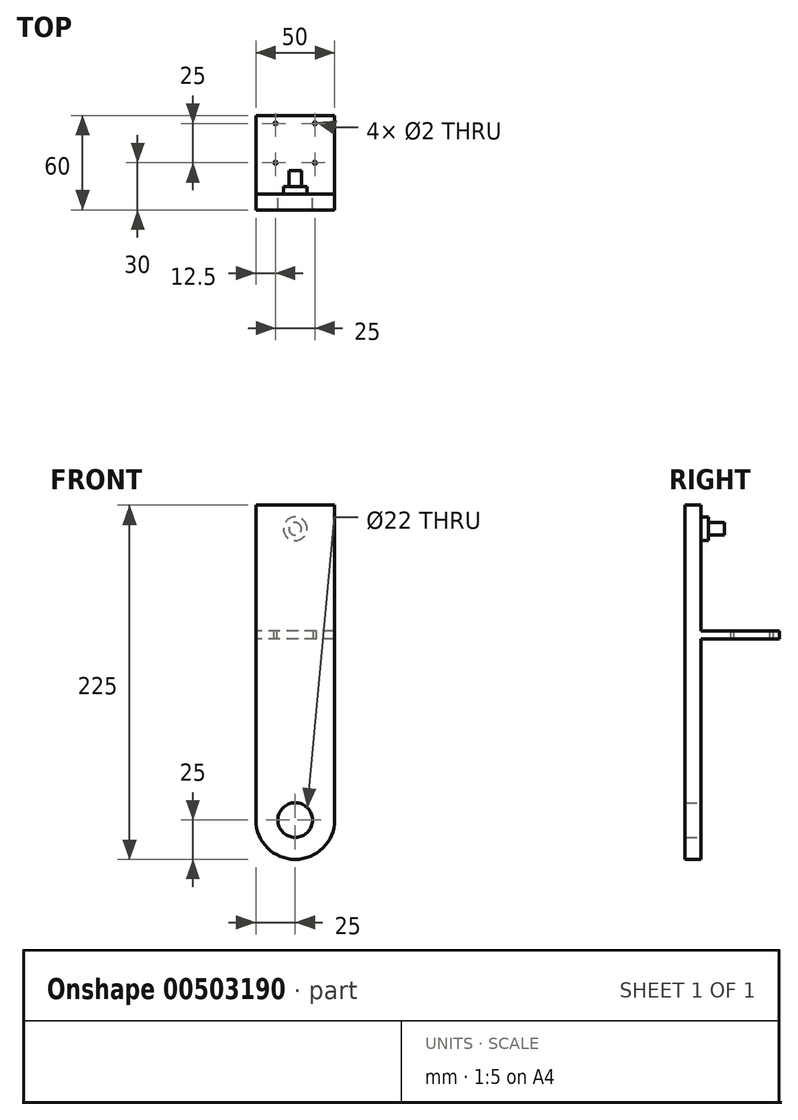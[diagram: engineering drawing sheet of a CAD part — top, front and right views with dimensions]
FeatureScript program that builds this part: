
annotation { "Feature Type Name" : "Feature", "Feature Type Description" : "" }
export const myFeature = defineFeature(function(context is Context, id is Id, definition is map)
    precondition{}
    {
        {
            var Q0;
            Q0=qCreatedBy(makeId("Front.planeOp"),FACE);
            var sketch = newSketch(context, id + "F0", { "sketchPlane" : qUnion([Q0])});
            skCircle(sketch, "E0", {"center": v(0, 0) * mm, "radius": 11 * mm});
            skArc(sketch, "E1", {"start": v(-25, 0) * mm, "mid": v(0, -25) * mm, "end": v(25, 0) * mm});
            skLineSegment(sketch, "E2", {"start": v(-25, 0) * mm, "end": v(-25, 200) * mm});
            skLineSegment(sketch, "E3", {"start": v(-25, 200) * mm, "end": v(25, 200) * mm});
            skLineSegment(sketch, "E4", {"start": v(25, 200) * mm, "end": v(25, 0) * mm});
            skLineSegment(sketch, "E5.bottom", {"start": v(25, 120) * mm, "end": v(-25, 120) * mm});
            skLineSegment(sketch, "E5.top", {"start": v(25, 115) * mm, "end": v(-25, 115) * mm});
            skLineSegment(sketch, "E5.left", {"start": v(25, 120) * mm, "end": v(25, 115) * mm});
            skLineSegment(sketch, "E5.right", {"start": v(-25, 120) * mm, "end": v(-25, 115) * mm});
            skCircle(sketch, "E6", {"center": v(0, 185) * mm, "radius": 7.5 * mm});
            skCircle(sketch, "E7", {"center": v(0, 185) * mm, "radius": 4 * mm});
            skSolve(sketch);
        }
        {
            var Q0;
            Q0=makeQuery(id+"F0.imprint","IMPRINT",FACE,{"disambiguationData":[TD([[makeQuery(id+"F0.imprint","IMPRINT",EDGE,{"derivedFrom":sQuery(id+"F0.wireOp",EDGE,"E0")}),-1.0]])]});
            var Q1;
            Q1=makeQuery(id+"F0.imprint","IMPRINT",FACE,{"disambiguationData":[TD([[makeQuery(id+"F0.imprint","IMPRINT",EDGE,{"derivedFrom":sQuery(id+"F0.wireOp",EDGE,"E5.bottom")}),1.0]])]});
            var Q2;
            {var subQ2=sQuery(id+"F0.wireOp",EDGE,"E3");Q2=makeQuery(id+"F0.imprint","IMPRINT",FACE,{"disambiguationData":[TD([[makeQuery(id+"F0.imprint","IMPRINT",EDGE,{"derivedFrom":subQ2}),-1.0]])]});}
            var Q3;
            Q3=makeQuery(id+"F0.imprint","IMPRINT",FACE,{"disambiguationData":[TD([[makeQuery(id+"F0.imprint","IMPRINT",EDGE,{"derivedFrom":sQuery(id+"F0.wireOp",EDGE,"E6")}),1.0]])]});
            var Q4;
            Q4=makeQuery(id+"F0.imprint","IMPRINT",FACE,{"disambiguationData":[TD([[makeQuery(id+"F0.imprint","IMPRINT",EDGE,{"derivedFrom":sQuery(id+"F0.wireOp",EDGE,"E7")}),1.0]])]});
            extrude(context, id + "F1", {"entities" : qUnion([Q0, Q1, Q2, Q3, Q4]), "depth" : 10 * mm});
        }
        {
            var Q0;
            Q0=makeQuery(id+"F0.imprint","IMPRINT",FACE,{"disambiguationData":[TD([[makeQuery(id+"F0.imprint","IMPRINT",EDGE,{"derivedFrom":sQuery(id+"F0.wireOp",EDGE,"E5.bottom")}),1.0]])]});
            extrude(context, id + "F2", {"entities" : qUnion([Q0]), "operationType" : NewBodyOperationType.ADD, "oppositeDirection" : true, "depth" : 50 * mm});
        }
        {
            var Q0;
            Q0=makeQuery(id+"F2.opExtrude","SWEPT_FACE",FACE,{"disambiguationData":[OSD([sQuery(id+"F0.wireOp",EDGE,"E5.bottom")])]});
            var sketch = newSketch(context, id + "F3", { "sketchPlane" : qUnion([Q0])});
            skLineSegment(sketch, "E8.bottom", {"start": v(-12.5, 20) * mm, "end": v(12.5, 20) * mm, "construction": true});
            skLineSegment(sketch, "E8.top", {"start": v(-12.5, 45) * mm, "end": v(12.5, 45) * mm, "construction": true});
            skLineSegment(sketch, "E8.left", {"start": v(-12.5, 20) * mm, "end": v(-12.5, 45) * mm, "construction": true});
            skLineSegment(sketch, "E8.right", {"start": v(12.5, 20) * mm, "end": v(12.5, 45) * mm, "construction": true});
            skCircle(sketch, "E9", {"center": v(-12.5, 20) * mm, "radius": 1 * mm});
            skCircle(sketch, "E10", {"center": v(-12.5, 45) * mm, "radius": 1 * mm});
            skCircle(sketch, "E11", {"center": v(12.5, 20) * mm, "radius": 1 * mm});
            skCircle(sketch, "E12", {"center": v(12.5, 45) * mm, "radius": 1 * mm});
            skSolve(sketch);
        }
        {
            var Q0;
            Q0=makeQuery(id+"F3.imprint","IMPRINT",FACE,{"disambiguationData":[TD([[makeQuery(id+"F3.imprint","IMPRINT",EDGE,{"derivedFrom":sQuery(id+"F3.wireOp",EDGE,"E9")}),1.0]])]});
            var Q1;
            Q1=makeQuery(id+"F3.imprint","IMPRINT",FACE,{"disambiguationData":[TD([[makeQuery(id+"F3.imprint","IMPRINT",EDGE,{"derivedFrom":sQuery(id+"F3.wireOp",EDGE,"E10")}),1.0]])]});
            var Q2;
            Q2=makeQuery(id+"F3.imprint","IMPRINT",FACE,{"disambiguationData":[TD([[makeQuery(id+"F3.imprint","IMPRINT",EDGE,{"derivedFrom":sQuery(id+"F3.wireOp",EDGE,"E12")}),1.0]])]});
            var Q3;
            Q3=makeQuery(id+"F3.imprint","IMPRINT",FACE,{"disambiguationData":[TD([[makeQuery(id+"F3.imprint","IMPRINT",EDGE,{"derivedFrom":sQuery(id+"F3.wireOp",EDGE,"E11")}),1.0]])]});
            extrude(context, id + "F4", {"entities" : qUnion([Q0, Q1, Q2, Q3]), "operationType" : NewBodyOperationType.REMOVE, "oppositeDirection" : true, "depth" : 25 * mm});
        }
        {
            var Q0;
            Q0=makeQuery(id+"F0.imprint","IMPRINT",FACE,{"disambiguationData":[TD([[makeQuery(id+"F0.imprint","IMPRINT",EDGE,{"derivedFrom":sQuery(id+"F0.wireOp",EDGE,"E6")}),1.0]])]});
            extrude(context, id + "F5", {"entities" : qUnion([Q0]), "operationType" : NewBodyOperationType.ADD, "oppositeDirection" : true, "depth" : 5 * mm});
        }
        {
            var Q0;
            Q0=makeQuery(id+"F0.imprint","IMPRINT",FACE,{"disambiguationData":[TD([[makeQuery(id+"F0.imprint","IMPRINT",EDGE,{"derivedFrom":sQuery(id+"F0.wireOp",EDGE,"E7")}),1.0]])]});
            extrude(context, id + "F6", {"entities" : qUnion([Q0]), "operationType" : NewBodyOperationType.ADD, "oppositeDirection" : true, "depth" : 15 * mm});
        }
    });
